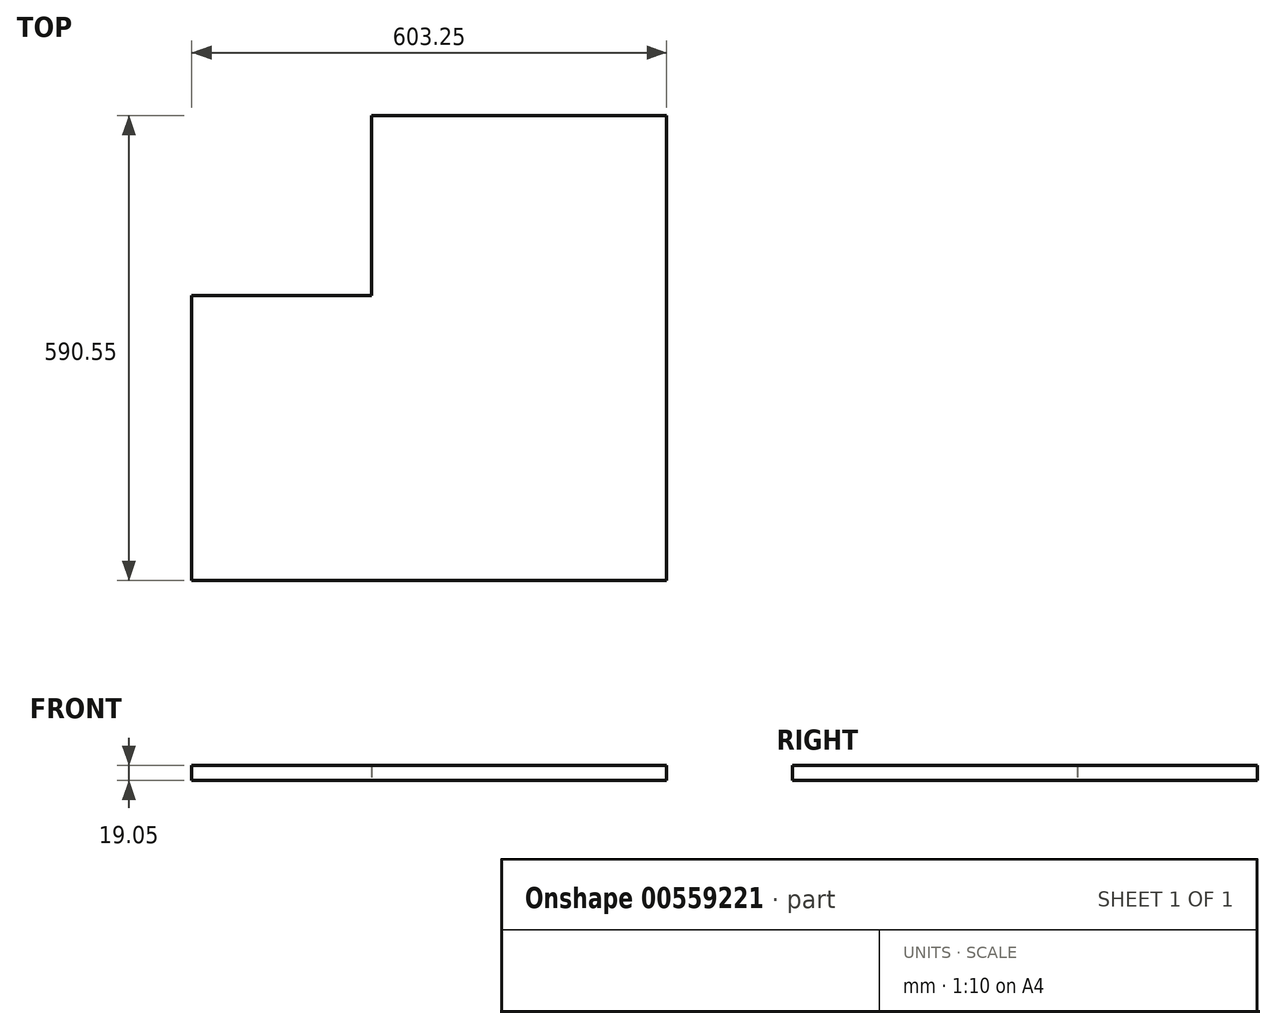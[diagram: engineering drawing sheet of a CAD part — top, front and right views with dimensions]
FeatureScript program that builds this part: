
annotation { "Feature Type Name" : "Feature", "Feature Type Description" : "" }
export const myFeature = defineFeature(function(context is Context, id is Id, definition is map)
    precondition{}
    {
        {
            var Q0;
            Q0=qCreatedBy(makeId("Top.planeOp"),FACE);
            var sketch = newSketch(context, id + "F0", { "sketchPlane" : qUnion([Q0])});
            skLineSegment(sketch, "E0.bottom", {"start": v(0, 0) * mm, "end": v(603.25, 0) * mm});
            skLineSegment(sketch, "E0.top", {"start": v(0, 590.55) * mm, "end": v(603.25, 590.55) * mm});
            skLineSegment(sketch, "E0.left", {"start": v(0, 0) * mm, "end": v(0, 590.55) * mm});
            skLineSegment(sketch, "E0.right", {"start": v(603.25, 0) * mm, "end": v(603.25, 590.55) * mm});
            skLineSegment(sketch, "E1", {"start": v(0, 361.95) * mm, "end": v(228.6, 361.95) * mm});
            skLineSegment(sketch, "E2", {"start": v(228.6, 361.95) * mm, "end": v(228.6, 590.55) * mm});
            skPoint(sketch, "E2.endSnap0", {"position": v(301.62, 590.55) * mm});
            skSolve(sketch);
        }
        {
            var Q0;
            Q0=makeQuery(id+"F0.imprint","IMPRINT",FACE,{"disambiguationData":[TD([[makeQuery(id+"F0.imprint","IMPRINT",EDGE,{"derivedFrom":sQuery(id+"F0.wireOp",EDGE,"E0.bottom")}),1.0]])]});
            extrude(context, id + "F1", {"entities" : qUnion([Q0]), "depth" : 19.05 * mm, "offsetDistance" : 25.4 * mm});
        }
    });
